# Revit family: Zumtobel PANOS INF SC R100
name_source: partatom
category: Lighting Fixtures
revit_build: Autodesk Revit 2016 (Build: 20150220_1215(x64)
units: mm (PartAtom-declared; Revit-internal decimal feet)

## family parameters
Cut with Voids When Loaded = No
Host = Face
Light Source = Yes
OmniClass Number = 23.80.70.11
OmniClass Title = Luminaries for Internal Lighting
Part Type = Normal
Room Calculation Point = No
Round Connector Dimension = Use Diameter
Shared = No

## types (2) — shared parameters
Assembly Code = D5020200
Body = Zumtobel_Metal_White
Color Filter = 16777215
Description = LED luminaire
Dimming Lamp Color Temperature Shift = <None>
Lamp = LED
Manufacturer = Zumtobel Lighting
Tilt Angle = 180.00°
URL = http://www.zumtobel.com
Voltage = 230 V
zero-valued in all types: Default Elevation

## per-type parameters (varying)
| type | Apparent Load | Height | Length | Model | Photometric Web File | Width |
| PANOS-INF SC R100 | 22 VA | 276 mm  [stored 0.905512 ft] | 100 mm  [stored 0.328084 ft] | 60818411 | 60818411_(STD_LEO).IES | 100 mm  [stored 0.328084 ft] |
| PANOS-INF SC R70 | 12 VA | 227 mm  [stored 0.744751 ft] | 70 mm  [stored 0.229659 ft] | 60818364 | 60818364_(STD_LEO).IES | 70 mm  [stored 0.229659 ft] |

note: [stored X ft] marks values corroborated as IEEE doubles in the binary element streams (Revit-internal decimal feet)

## geometry (parser evidence)
native form markers: Sweep x5
no freeform markers — native parametric forms only
